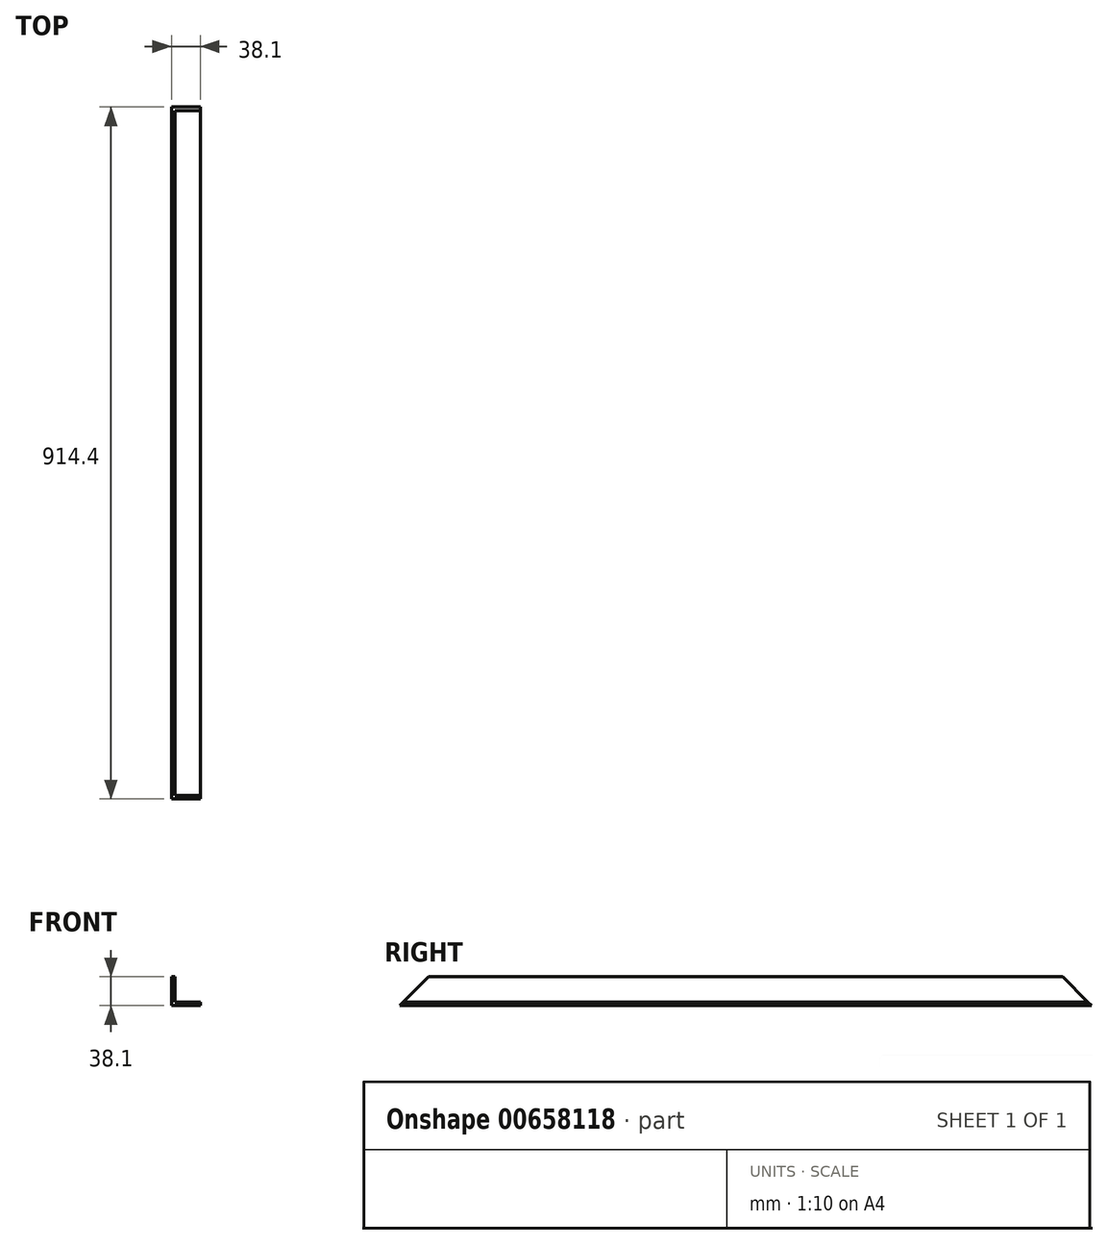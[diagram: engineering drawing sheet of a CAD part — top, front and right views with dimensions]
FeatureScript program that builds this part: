
annotation { "Feature Type Name" : "Feature", "Feature Type Description" : "" }
export const myFeature = defineFeature(function(context is Context, id is Id, definition is map)
    precondition{}
    {
        {
            var Q0;
            Q0=qCreatedBy(makeId("Front.planeOp"),FACE);
            var sketch = newSketch(context, id + "F0", { "sketchPlane" : qUnion([Q0])});
            skLineSegment(sketch, "E0", {"start": v(0, 0) * mm, "end": v(0, 38.1) * mm});
            skLineSegment(sketch, "E1", {"start": v(0, 38.1) * mm, "end": v(4.76, 38.1) * mm});
            skLineSegment(sketch, "E2", {"start": v(4.76, 38.1) * mm, "end": v(4.76, 4.76) * mm});
            skLineSegment(sketch, "E3", {"start": v(4.76, 4.76) * mm, "end": v(38.1, 4.76) * mm});
            skLineSegment(sketch, "E4", {"start": v(38.1, 4.76) * mm, "end": v(38.1, 0) * mm});
            skLineSegment(sketch, "E5", {"start": v(38.1, 0) * mm, "end": v(0, 0) * mm});
            skSolve(sketch);
        }
        {
            var Q0;
            Q0=qSketchRegion(id+"F0",true);
            extrude(context, id + "F1", {"entities" : qUnion([Q0]), "oppositeDirection" : true, "depth" : 914.4 * mm, "offsetDistance" : 25.4 * mm});
        }
        {
            var Q0;
            Q0=makeQuery(id+"F1.opExtrude","SWEPT_FACE",FACE,{"disambiguationData":[OSD([sQuery(id+"F0.wireOp",EDGE,"E0")])]});
            var sketch = newSketch(context, id + "F2", { "sketchPlane" : qUnion([Q0])});
            skLineSegment(sketch, "E6.0", {"start": v(-914.4, 38.1) * mm, "end": v(0, 38.1) * mm});
            skLineSegment(sketch, "E6.1", {"start": v(-914.4, 0) * mm, "end": v(-914.4, 38.1) * mm});
            skLineSegment(sketch, "E6.2", {"start": v(0, 0) * mm, "end": v(0, 38.1) * mm});
            skLineSegment(sketch, "E7", {"start": v(0, 0) * mm, "end": v(-38.1, 38.1) * mm});
            skLineSegment(sketch, "E8", {"start": v(-914.4, 0) * mm, "end": v(-876.3, 38.1) * mm});
            skSolve(sketch);
        }
        {
            var Q0;
            Q0=qSketchRegion(id+"F2",true);
            extrude(context, id + "F3", {"entities" : qUnion([Q0]), "operationType" : NewBodyOperationType.REMOVE, "endBound" : BoundingType.THROUGH_ALL, "oppositeDirection" : true, "depth" : 25.4 * mm, "offsetDistance" : 25.4 * mm});
        }
    });
